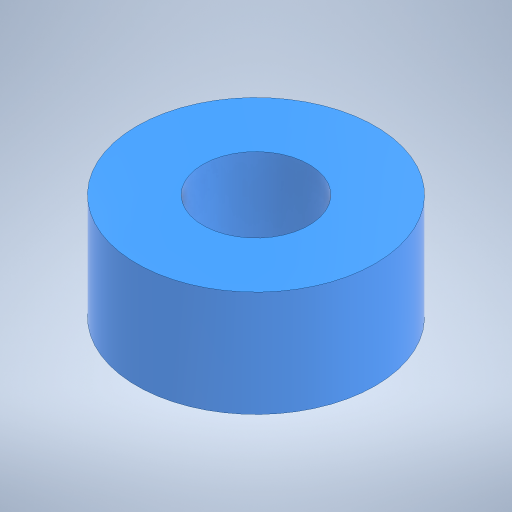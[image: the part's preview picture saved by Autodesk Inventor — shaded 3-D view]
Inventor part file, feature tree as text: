
AUTODESK INVENTOR PART (.ipt)
format: ipt  version: 2024 (Build 280153000, 153)  size: 211,968 bytes
history: native  units: in
note: dims shown in document units (in); Inventor stores cm internally (conversion verified against a paired STEP export)
features: extrude x1, sketch x1
ambient origin geometry x8: Origin, YZ Plane, XZ Plane, XY Plane, X Axis, Y Axis, Z Axis, Center Point
bodies: Solid1 (feature_tree)
feature tree (2):
  extrude  "Extrusion1"  Depth=0.5in
  sketch  "Sketch1"  dims[d0=1.125in d1=0.5in d2=0.5in d3=0.0in]
